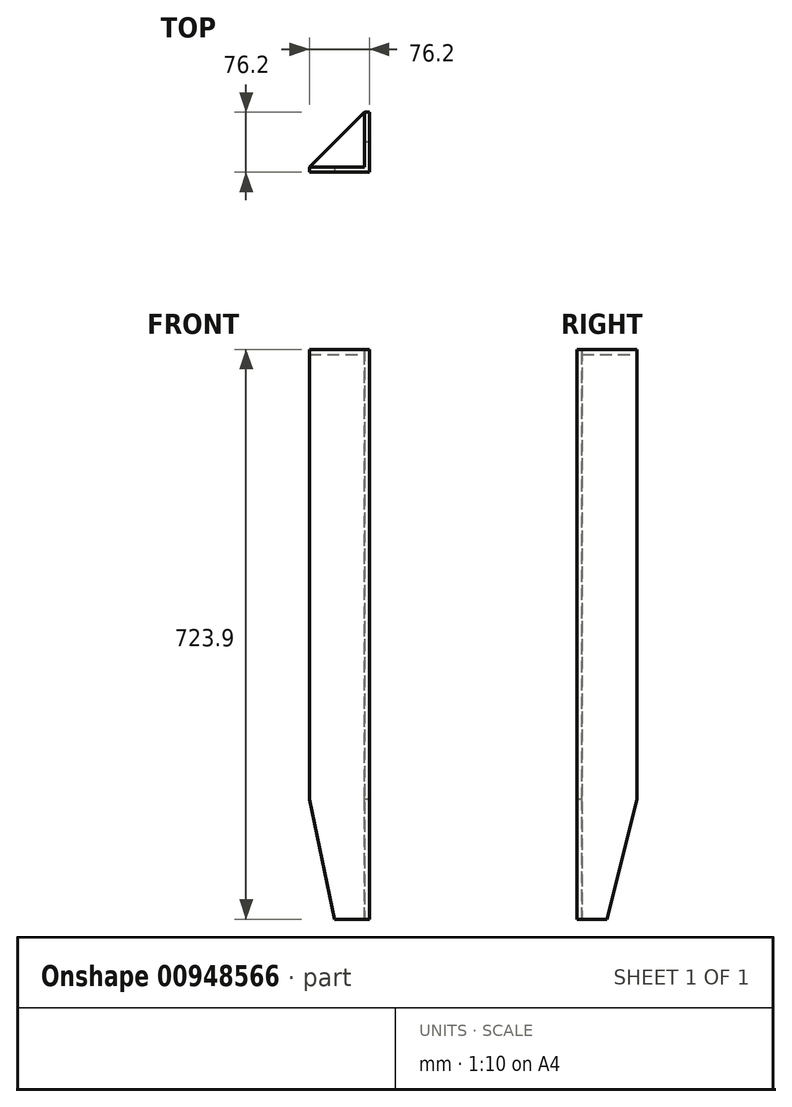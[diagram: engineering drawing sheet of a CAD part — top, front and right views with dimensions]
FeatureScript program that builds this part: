
annotation { "Feature Type Name" : "Feature", "Feature Type Description" : "" }
export const myFeature = defineFeature(function(context is Context, id is Id, definition is map)
    precondition{}
    {
        {
            var Q0;
            Q0=qCreatedBy(makeId("Right.planeOp"),FACE);
            var sketch = newSketch(context, id + "F0", { "sketchPlane" : qUnion([Q0])});
            skLineSegment(sketch, "E0", {"start": v(0, 0) * mm, "end": v(38.1, 0) * mm});
            skLineSegment(sketch, "E1", {"start": v(38.1, 0) * mm, "end": v(76.2, 152.4) * mm});
            skLineSegment(sketch, "E2", {"start": v(76.2, 152.4) * mm, "end": v(76.2, 723.9) * mm});
            skLineSegment(sketch, "E3", {"start": v(76.2, 723.9) * mm, "end": v(0, 723.9) * mm});
            skLineSegment(sketch, "E4", {"start": v(0, 723.9) * mm, "end": v(0, 0) * mm});
            skSolve(sketch);
        }
        {
            var Q0;
            Q0=makeQuery(id+"F0.imprint","IMPRINT",FACE,{"disambiguationData":[TD([[makeQuery(id+"F0.imprint","IMPRINT",EDGE,{"derivedFrom":sQuery(id+"F0.wireOp",EDGE,"E0")}),1.0]])]});
            extrude(context, id + "F1", {"entities" : qUnion([Q0]), "depth" : 6.35 * mm, "offsetDistance" : 25.4 * mm});
        }
        {
            var Q0;
            Q0=qCreatedBy(makeId("Front.planeOp"),FACE);
            var sketch = newSketch(context, id + "F2", { "sketchPlane" : qUnion([Q0])});
            skLineSegment(sketch, "E5", {"start": v(6.35, 0) * mm, "end": v(-38.1, 0) * mm});
            skLineSegment(sketch, "E6", {"start": v(-38.1, 0) * mm, "end": v(-69.85, 152.4) * mm});
            skLineSegment(sketch, "E7", {"start": v(-69.85, 152.4) * mm, "end": v(-69.85, 723.9) * mm});
            skLineSegment(sketch, "E8", {"start": v(-69.85, 723.9) * mm, "end": v(6.35, 723.9) * mm});
            skLineSegment(sketch, "E9", {"start": v(6.35, 723.9) * mm, "end": v(6.35, 0) * mm});
            skSolve(sketch);
        }
        {
            var Q0;
            Q0=makeQuery(id+"F2.imprint","IMPRINT",FACE,{"disambiguationData":[TD([[makeQuery(id+"F2.imprint","IMPRINT",EDGE,{"derivedFrom":sQuery(id+"F2.wireOp",EDGE,"E5")}),-1.0]])]});
            extrude(context, id + "F3", {"entities" : qUnion([Q0]), "operationType" : NewBodyOperationType.ADD, "oppositeDirection" : true, "depth" : 6.35 * mm, "offsetDistance" : 25.4 * mm});
        }
        {
            var Q0;
            Q0=makeQuery(id+"F3.boolean.opBoolean","MERGE",FACE,{"derivedFrom":[makeQuery(id+"F1.opExtrude","SWEPT_FACE",FACE,{"disambiguationData":[OSD([sQuery(id+"F0.wireOp",EDGE,"E3")])]}),makeQuery(id+"F3.opExtrude","SWEPT_FACE",FACE,{"disambiguationData":[OSD([sQuery(id+"F2.wireOp",EDGE,"E8")])]})]});
            var sketch = newSketch(context, id + "F4", { "sketchPlane" : qUnion([Q0])});
            skLineSegment(sketch, "E10", {"start": v(-69.85, 6.35) * mm, "end": v(0, 76.2) * mm});
            skSolve(sketch);
        }
        {
            var Q0;
            Q0=makeQuery(id+"F4.imprint","IMPRINT",FACE,{"disambiguationData":[TD([[makeQuery(id+"F4.imprint","IMPRINT",EDGE,{"derivedFrom":sQuery(id+"F4.wireOp",EDGE,"E10")}),-1.0]])]});
            extrude(context, id + "F5", {"entities" : qUnion([Q0]), "oppositeDirection" : true, "depth" : 6.35 * mm, "offsetDistance" : 25.4 * mm});
        }
    });
